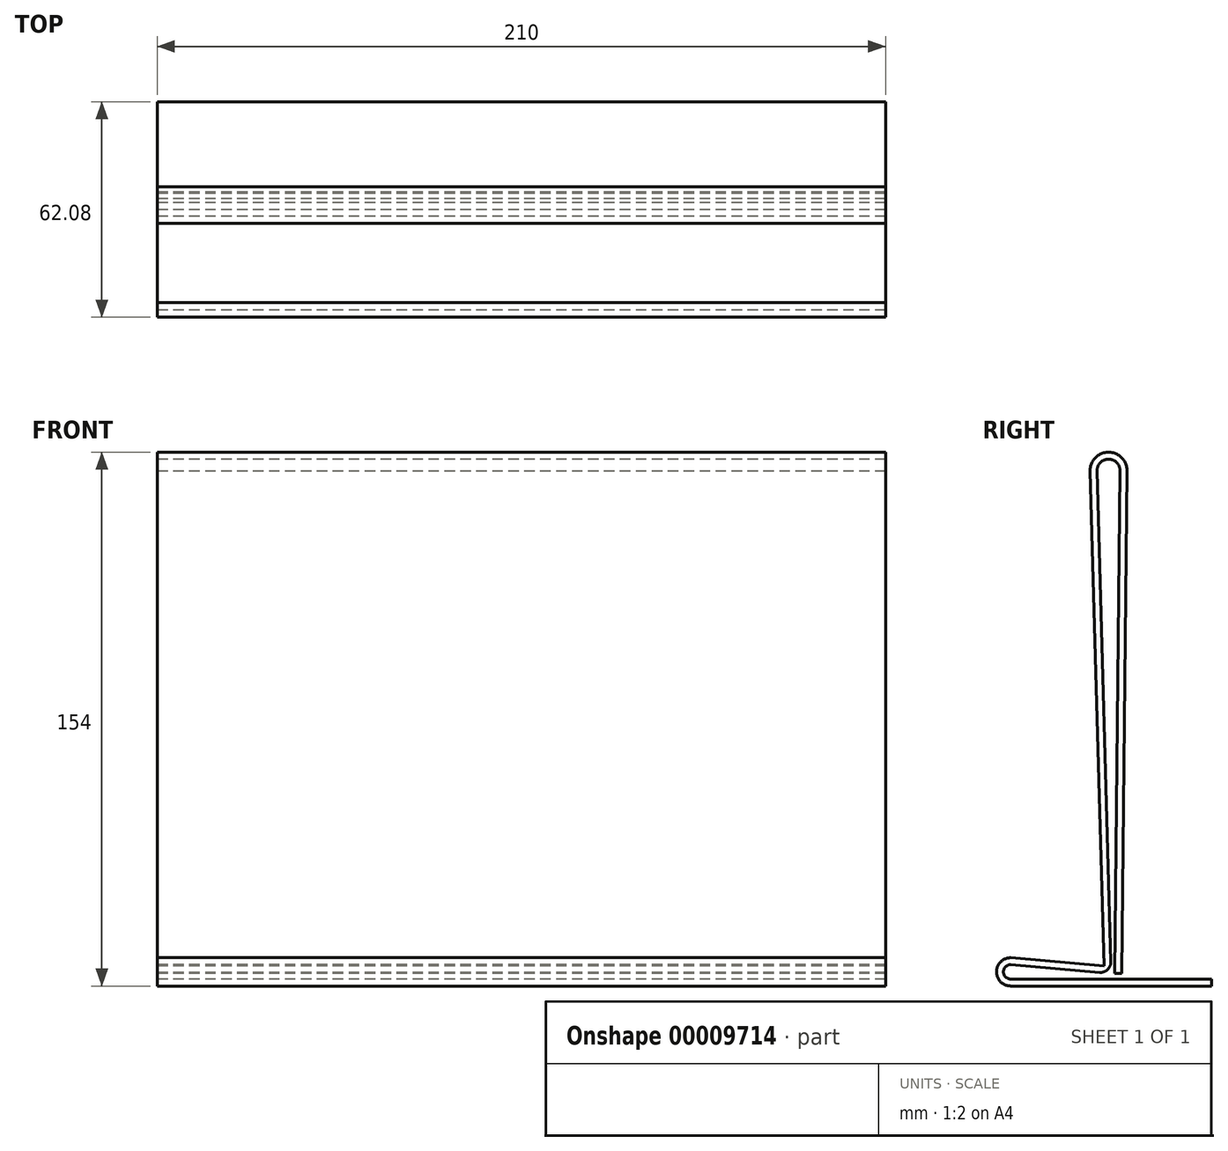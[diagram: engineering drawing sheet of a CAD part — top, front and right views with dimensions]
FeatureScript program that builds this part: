
annotation { "Feature Type Name" : "Feature", "Feature Type Description" : "" }
export const myFeature = defineFeature(function(context is Context, id is Id, definition is map)
    precondition{}
    {
        {
            var Q0;
            Q0=qCreatedBy(makeId("Right.planeOp"),FACE);
            var sketch = newSketch(context, id + "F0", { "sketchPlane" : qUnion([Q0])});
            skLineSegment(sketch, "E0", {"start": v(29, -35.05) * mm, "end": v(-29, -35.05) * mm});
            skArc(sketch, "E1", {"start": v(-29, -30.9) * mm, "mid": v(-31.08, -32.97) * mm, "end": v(-29, -35.05) * mm});
            skLineSegment(sketch, "E2", {"start": v(-29, -30.9) * mm, "end": v(-3.35, -33.11) * mm});
            skLineSegment(sketch, "E3", {"start": v(-0.1, -30.04) * mm, "end": v(-4.07, 111.55) * mm});
            skArc(sketch, "E4", {"start": v(2.55, 111.55) * mm, "mid": v(-0.76, 114.95) * mm, "end": v(-4.07, 111.55) * mm});
            skLineSegment(sketch, "E5", {"start": v(2.55, 111.55) * mm, "end": v(1.04, -33.4) * mm});
            skPoint(sketch, "E6.visualSharp", {"position": v(0, -33.4) * mm});
            skArc(sketch, "E6.filletArc", {"start": v(-3.35, -33.11) * mm, "mid": v(-1.03, -32.3) * mm, "end": v(-0.1, -30.04) * mm});
            skLineSegment(sketch, "E7.0", {"start": v(29, -37.05) * mm, "end": v(-29, -37.05) * mm});
            skArc(sketch, "E7.1", {"start": v(-28.9, -28.9) * mm, "mid": v(-33.08, -32.92) * mm, "end": v(-29, -37.05) * mm});
            skLineSegment(sketch, "E7.2", {"start": v(-28.9, -28.9) * mm, "end": v(-2.06, -31.22) * mm});
            skLineSegment(sketch, "E7.3", {"start": v(-2.06, -31.22) * mm, "end": v(-6.07, 111.5) * mm});
            skArc(sketch, "E7.4", {"start": v(4.55, 111.51) * mm, "mid": v(-0.77, 116.95) * mm, "end": v(-6.07, 111.5) * mm});
            skLineSegment(sketch, "E7.5", {"start": v(4.55, 111.51) * mm, "end": v(3.03, -33.43) * mm});
            skLineSegment(sketch, "E8", {"start": v(1.04, -33.4) * mm, "end": v(3.03, -33.43) * mm});
            skLineSegment(sketch, "E9", {"start": v(29, -35.05) * mm, "end": v(29, -37.05) * mm});
            skLineSegment(sketch, "E10", {"start": v(-0.76, 111.64) * mm, "end": v(-0.1, -30.04) * mm});
            skSolve(sketch);
        }
        {
            var Q0;
            Q0 = qSketchRegion(id + "F0", true);
            extrude(context, id + "F1", {"entities" : qUnion([Q0]), "depth" : 210 * mm});
        }
        {
            var Q0;
            Q0=sQuery(id+"F0.wireOp",EDGE,"E10");
            extrude(context, id + "F2", {"bodyType" : ToolBodyType.SURFACE, "surfaceEntities" : qUnion([Q0]), "depth" : 210 * mm});
        }
    });
